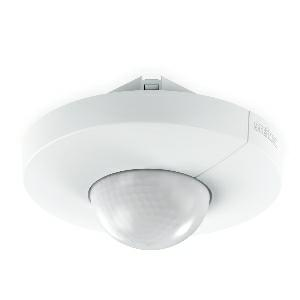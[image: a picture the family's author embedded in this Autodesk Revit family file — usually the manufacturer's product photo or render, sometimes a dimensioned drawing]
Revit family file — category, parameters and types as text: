
# Revit family: is_345_033811
name_source: partatom
category: Elektroinstallationen
revit_build: Autodesk Revit 2016 (Build: 20190508_0715(x64)
units: mm (PartAtom-declared; Revit-internal decimal feet)

## family parameters
Basisbauteil = Fläche
Beim Laden mit Abzugskörper schneiden = Nein
Bemaßung runder Anschluss = Durchmesser verwenden
Beschriftungsausrichtung beibehalten = Nein
Gemeinsam genutzt = Nein
Raumberechnungspunkt = Nein
Teiletyp = Normal

## types (1)
- IS 345
    Apparent Load = 0 VA
    Beschreibung = Type: Motion detectors; Dimensions (Ø x H): 124 x 78 mm; Mains power supply: 220 – 240 V / 50 – 60 Hz; Sensor Technology: passive infrared; Application, place: Indoors; Application, room: corridor / aisle, multi-storey / underground car park, Indoors; Installation site: ceiling; Installation: Concealed wiring; Switching zones: 280 switching zones; Electronic scalability: No; Mechanical scalability: No; Mounting height: 2,50 – 5,00 m; Optimum mounting height: 2,8 m; Detection angle: 360 °; Angle of aperture: 45 °; Sneak-by guard: Yes; Capability of masking out individual segments: Yes; Reach, radial: 12 x 4 m (48 m²); Reach, tangential: 23 x 4 m (92 m²); Twilight setting TEACH: Yes; Twilight setting: 2 – 1000 lx; Time setting: 5 sec – 15 min; Switching output 1, resistive: 2000 W; Switching output 1, number of LEDs / fluorescent lamps: 8 pcs.; Constant-lighting control: No; Basic light level function: No; Functions: Normal / test mode, Manual ON / ON-OFF; Settings via: Remote control, Potentiometers, Smart Remote; With remote control: No; Interconnection: Yes; IP-rating: IP20; Material: Plastic; Ambient temperature: -20 – 50 °C; Colour: white; Colour, RAL: 9003; Manufacturer's Warranty: 5 years; Version: COM1 - concealed, rd.; PU1, EAN: 4007841033811
    Height = 0 mm  [stored 0 ft]
    Hersteller = Steinel
    Length = 124 mm  [stored 0.406824 ft]
    Maximum range = 11.589 m
    ModVariant = Nein
    Modell = 033811
    Mounting Place = Ceiling
    Mounting Type = Recessed
    Number of Poles = 1
    OnlyDefault = Ja
    Power Factor = 1
    Product Name = IS 345
    Product group = Presence detector
    ProductGroupID = 4
    Protection Class = Protection class
    Protection Degree = IP 20
    RlxData = <blob elided: 156565 chars, md5=11f5470f>
    Sensor characteristics = Stretched
    Sensor type = Passive (infrared)
    SensorDataFile = <blob elided: 5885 chars, md5=98bccc25>
    Type of entry = Motion
    Typenbild = produkt1_033811.jpg
    Typenkommentare = Product without accessories
    URL = http://relux.com
    VarID = ---
    Voltage = 0 V
    Vorgabe-Ansicht = 1800 mm
    Weight = 0.00 kg
    Width = 0 mm  [stored 0 ft]

note: [stored X ft] marks values corroborated as IEEE doubles in the binary element streams (Revit-internal decimal feet)

## geometry (parser evidence)
native form markers: Blend x4, Sweep x17
no freeform markers — native parametric forms only
